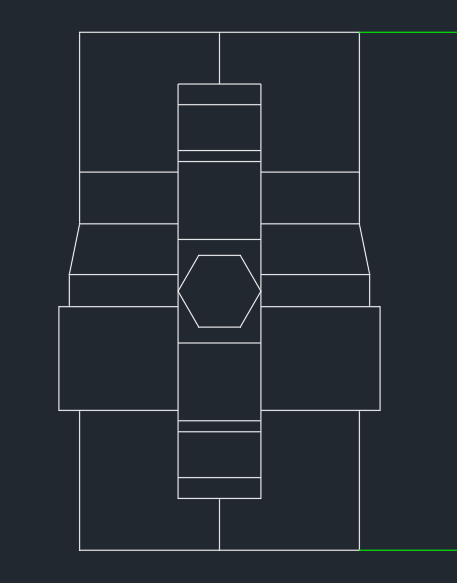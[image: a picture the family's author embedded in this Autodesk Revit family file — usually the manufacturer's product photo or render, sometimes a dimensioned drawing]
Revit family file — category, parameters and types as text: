
# Revit family: 003L1117 ШКСО-1Р - П
name_source: partatom
category: Pipe Fittings
units: mm (PartAtom-declared; Revit-internal decimal feet)

## family parameters
Always vertical = Yes
Cut with Voids When Loaded = No
Part Type = Multi Port
Round Connector Dimension = Use Diameter
Shared = No
Work Plane-Based = No

## types (1)
- 7-выходов
    ADSK_Единица измерения = компл.
    ADSK_Завод-изготовитель = Danfoss
    ADSK_Количество = 1
    ADSK_Масса = 0
    ADSK_Наименование = Квартирная станция
    DN = 32 mm  [stored 0.104987 ft]
    Default Elevation = 0 mm  [stored 0 ft]
    K Coefficient = 1
    Loss Method = Not Defined
    Manufacturer = Danfoss
    URL = https://ru.giacomini.com
    dn vn = 28 mm  [stored 0.0918635 ft]
    Вставка под счетчик = 110 mm  [stored 0.360892 ft]
    Вылет от стенки обратка = 85 mm  [stored 0.278871 ft]
    Материал корпуса = Фильтр_Латунь
    Материал пластик зеленый = Plastic, Green
    Материал пластика белый = Plastic, White
    Материал пластика красный = Plastic, Red
    Между осями коллектора = 213 mm  [stored 0.698819 ft]
    Отступ коллектора Т1 слева = 600 mm  [stored 1.9685 ft]
    УГОЛ = 45.00°
    Уровень оси коллектора = 250 mm  [stored 0.82021 ft]
    вылет от колл = 40 mm  [stored 0.131234 ft]
    вылет от стенки пода = 48 mm  [stored 0.15748 ft]
    длина узла перед подачей = 210 mm  [stored 0.688976 ft]
    отступ от края до оси врезки = 30 mm  [stored 0.0984252 ft]
    смещ массива обратки = 250 mm  [stored 0.82021 ft]
    смещ массива подачи = 463 mm  [stored 1.51903 ft]
    шаг = 100 mm  [stored 0.328084 ft]

note: [stored X ft] marks values corroborated as IEEE doubles in the binary element streams (Revit-internal decimal feet)

## geometry (parser evidence)
native form markers: Blend x57, Sweep x2
no freeform markers — native parametric forms only
